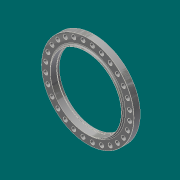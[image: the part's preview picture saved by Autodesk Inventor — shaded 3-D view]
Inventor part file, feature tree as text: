
AUTODESK INVENTOR PART (.ipt)
format: ipt  version: 2017.3 (Build 213256000, 256)  size: 305,152 bytes
history: native  units: in
note: dims shown in document units (in); Inventor stores cm internally (conversion verified against a paired STEP export)
features: sketch x6, extrude x3, chamfer x3, fillet x2, hole x1, pattern_circular x1, plane x1, loft x1, revolve x1, other x1
ambient origin geometry x8: Origin, YZ Plane, XZ Plane, XY Plane, X Axis, Y Axis, Z Axis, Center Point
bodies: Solid1 (feature_tree)
feature tree (20):
  extrude  "Extrusion1"  Depth=3.0in TaperAngle=0.0deg
  hole  "Hole1"  [1 undecoded]
  chamfer  "Chamfer1"  Distance=11.0236in Angle=360.0deg
  pattern_circular  "Circular Pattern1"  [2 undecoded]
  chamfer  "Chamfer2"  Distance=30.0in
  sketch  "Sketch3"  dims[d5=1.875in d6=0.75in d7=0.375in d8=0.25in d9=0.5635in d10=1.0in d11=0.8108in d12=11.0236in d13=360.0deg]
  plane  "Work Plane1"
  extrude  "Extrusion2"  Depth=0.5in TaperAngle=0.0deg
  loft  "Loft1"
  fillet  "Fillet1"  [1 undecoded]
  revolve  "Revolution1"  [1 undecoded]
  extrude  "Extrusion3"  Depth=0.0312in
  chamfer  "Chamfer3"  Distance=0.5in
  fillet  "Fillet2"  Radius=0.4375in
  sketch  "Sketch1"  dims[d0=43.0in d1=3.0in d2=0.0in]
  sketch  "Sketch2"  dims[d3=39.25in d4=0.0442in]
  sketch  "Sketch4"  dims[d15=0.0625in d16=0.125in d17=45.0deg]
  other  "Edges1"
  sketch  "Sketch5"  dims[d18=0.0625in d19=0.125in d20=45.0deg]
  sketch  "Sketch6"  dims[d21=35.25in d22=6.0in d23=30.0in d24=0.5in d25=0.0in d26=0.0in d27=90.0deg d28=0.0in d29=90.0deg d30=0.5in d31=34.0in d32=0.5in d33=0.4375in d34=0.2577in d35=0.5in d36=3.875in d37=0.0393in d38=90.0deg d39=32.5in d40=1.0in d41=0.0in d42=0.0312in d43=0.125in d44=45.0deg d45=0.0312in]
note: 5 required parameter values undecoded (feature->parameter linkage not recoverable at this tier; creation-order binding heuristic only, values carry confidence <= 0.55)